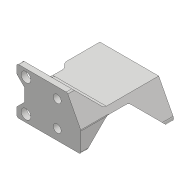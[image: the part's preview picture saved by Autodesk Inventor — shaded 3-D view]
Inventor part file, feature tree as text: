
AUTODESK INVENTOR PART (.ipt)
format: ipt  version: 2018 (Build 220112000, 112)  size: 731,136 bytes
history: native  units: mm
features: sketch x15, extrude x12, projected_geometry x10, fillet x5, hole x4, chamfer x3, mirror x2, plane x1
ambient origin geometry x8: Origin, YZ Plane, XZ Plane, XY Plane, X Axis, Y Axis, Z Axis, Center Point
bodies: Solid1 (feature_tree)
feature tree (52):
  extrude  "Extrusion1"  Depth=143.6mm
  hole  "Hole1"  [1 undecoded]
  extrude  "Extrusion2"  Depth=40.0mm
  extrude  "Extrusion5"  Depth=2.0mm
  extrude  "Extrusion3"  Depth=3.0mm TaperAngle=0.0deg
  extrude  "Extrusion4"  Depth=3.0mm TaperAngle=0.0deg
  sketch  "Sketch8"  dims[d18=41.0mm d20=3.0mm d21=0.0mm]
  hole  "Hole2"  [1 undecoded]
  hole  "Hole3"  [1 undecoded]
  extrude  "Extrusion6"  Depth=17.0624mm
  extrude  "Extrusion7"  Depth=2.0mm
  extrude  "Extrusion10"  Depth=3.0mm TaperAngle=0.0deg
  chamfer  "Chamfer3"  Distance=7.0mm
  plane  "Work Plane1"
  extrude  "Extrusion11"  Depth=2.0mm
  fillet  "Fillet1"  Radius=4.957359mm
  extrude  "Extrusion12"  Depth=2.0mm TaperAngle=0.0deg
  chamfer  "Chamfer4"  Distance=4.957359mm
  chamfer  "Chamfer5"  [1 undecoded]
  fillet  "Fillet2"  Radius=11.2mm
  fillet  "Fillet3"  Radius=10.0mm
  extrude  "Extrusion13"  [1 undecoded]
  fillet  "Fillet4"  Radius=8.0mm
  hole  "Hole4"  [1 undecoded]
  mirror  "Mirror2"
  extrude  "Extrusion14"  Depth=2.0mm
  fillet  "Fillet5"  Radius=9.5mm
  mirror  "Mirror3"
  sketch  "Sketch1"  dims[d0=76.0mm d1=143.6mm]
  sketch  "Sketch2"  dims[d2=3.0mm d3=0.0mm d4=8.0mm]
  sketch  "Sketch4"  dims[d5=70.0mm d6=40.0mm]
  sketch  "Sketch5"  dims[d7=3.2mm d8=6.0mm d9=6.3mm d10=2.0mm d11=90.0deg d12=8.0mm d13=20.594885mm d14=38.0mm]
  projected_geometry  "Projected Loop1"
  sketch  "Sketch7"  dims[d15=17.0mm d16=3.0mm d17=0.0mm]
  projected_geometry  "Projected Loop3"
  projected_geometry  "Projected Loop4"
  sketch  "Sketch10"  dims[d22=25.4mm d23=3.0mm d24=0.0mm]
  projected_geometry  "Projected Loop5"
  sketch  "Sketch11"  dims[d25=14.0mm d26=12.7mm]
  projected_geometry  "Projected Loop6"
  sketch  "Sketch12"  dims[d27=17.4625mm d30=17.0624mm]
  projected_geometry  "Projected Loop7"
  sketch  "Sketch16"  dims[d31=5.0mm]
  projected_geometry  "Projected Loop11"
  projected_geometry  "Projected Loop12"
  sketch  "Sketch17"  dims[d32=4.3mm d33=6.0mm d34=9.4mm d35=2.0mm d36=90.0deg d37=8.0mm d38=20.594885mm]
  projected_geometry  "Projected Loop13"
  sketch  "Sketch18"  dims[d39=5.3mm d40=6.0mm d41=10.4mm d42=2.0mm d43=90.0deg d44=8.0mm d45=20.594885mm d46=46.0mm]
  projected_geometry  "Projected Loop14"
  sketch  "Sketch19"  dims[d47=24.0mm d48=3.0mm d49=0.0mm]
  sketch  "Sketch20"  dims[d50=135.0deg]
  sketch  "Sketch21"  dims[d51=135.0deg d52=7.0mm d53=6.0mm d54=4.957359mm d55=50.0mm d56=0.0mm d57=4.957359mm d58=0.0mm d59=0.0mm d71=11.2mm d72=0.0mm d73=11.2mm d74=10.0mm d75=45.0deg d76=-18.0mm d77=8.0mm d78=8.0mm d79=9.5mm d80=9.5mm d81=15.0mm d82=0.0mm d83=2.0mm d84=18.0mm d85=15.0mm d86=0.0mm d87=15.0mm d88=10.0mm d89=45.0deg d90=4.24mm d91=10.0mm d92=45.0deg d93=1.0mm d94=3.0mm d95=15.0mm d96=0.0mm d97=1.0mm d98=26.0mm d99=10.0mm d100=12.0mm d101=2.459mm d102=6.0mm d103=10.4mm d104=2.0mm d105=90.0deg d106=10.0mm d107=20.594885mm d108=10.0mm d109=0.0mm d110=2.0mm]
note: 6 required parameter values undecoded (feature->parameter linkage not recoverable at this tier; creation-order binding heuristic only, values carry confidence <= 0.55)
